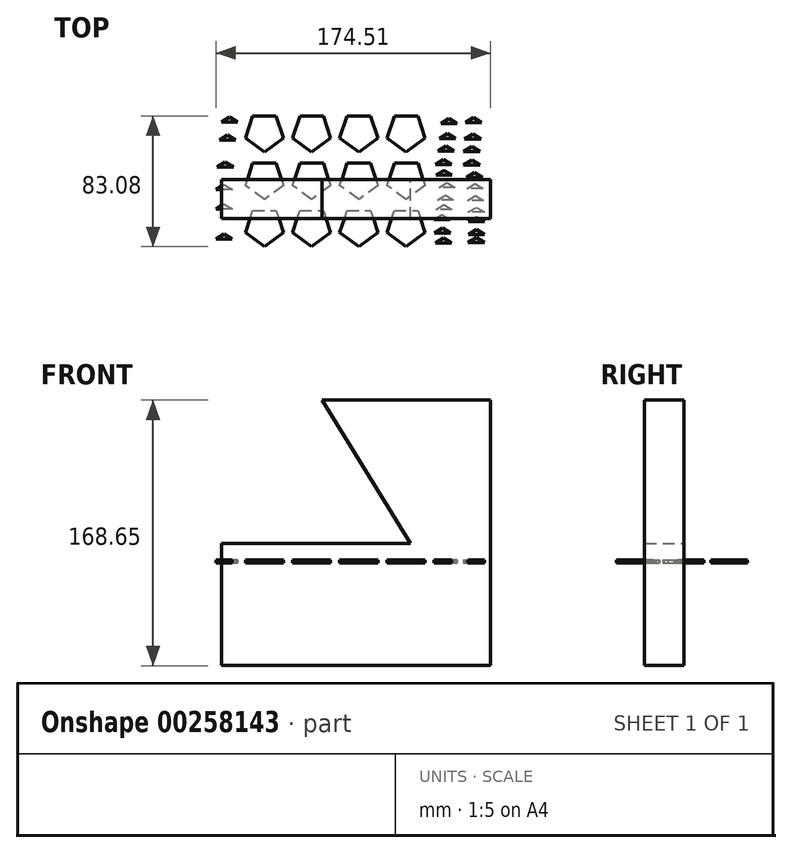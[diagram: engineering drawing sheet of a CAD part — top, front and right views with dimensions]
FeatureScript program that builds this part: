
annotation { "Feature Type Name" : "Feature", "Feature Type Description" : "" }
export const myFeature = defineFeature(function(context is Context, id is Id, definition is map)
    precondition{}
    {
        {
            var Q0;
            Q0=qCreatedBy(makeId("Top.planeOp"),FACE);
            var sketch = newSketch(context, id + "F0", { "sketchPlane" : qUnion([Q0])});
            skCircle(sketch, "E0.cCircle", {"center": v(30, 30) * mm, "radius": 10.32 * mm, "construction": true});
            skLineSegment(sketch, "E0.0", {"start": v(22.5, 40.32) * mm, "end": v(37.5, 40.32) * mm});
            skLineSegment(sketch, "E0.1", {"start": v(37.5, 40.32) * mm, "end": v(42.14, 26.06) * mm});
            skLineSegment(sketch, "E0.2", {"start": v(42.14, 26.06) * mm, "end": v(30, 17.24) * mm});
            skLineSegment(sketch, "E0.3", {"start": v(30, 17.24) * mm, "end": v(17.86, 26.06) * mm});
            skLineSegment(sketch, "E0.4", {"start": v(17.86, 26.06) * mm, "end": v(22.5, 40.32) * mm});
            skPoint(sketch, "E0.0.midPoint", {"position": v(30, 40.32) * mm});
            skLineSegment(sketch, "E1", {"start": v(52.02, 35.35) * mm, "end": v(57.12, 38.5) * mm});
            skLineSegment(sketch, "E2", {"start": v(57.12, 38.5) * mm, "end": v(62.23, 35.35) * mm});
            skLineSegment(sketch, "E3", {"start": v(62.23, 35.35) * mm, "end": v(52.02, 35.35) * mm});
            skCircle(sketch, "E4.cCircle", {"center": v(-60, 30) * mm, "radius": 10.32 * mm, "construction": true});
            skLineSegment(sketch, "E4.0", {"start": v(-67.5, 40.32) * mm, "end": v(-52.5, 40.32) * mm});
            skLineSegment(sketch, "E4.1", {"start": v(-52.5, 40.32) * mm, "end": v(-47.86, 26.06) * mm});
            skLineSegment(sketch, "E4.2", {"start": v(-47.86, 26.06) * mm, "end": v(-60, 17.24) * mm});
            skLineSegment(sketch, "E4.3", {"start": v(-60, 17.24) * mm, "end": v(-72.14, 26.06) * mm});
            skLineSegment(sketch, "E4.4", {"start": v(-72.14, 26.06) * mm, "end": v(-67.5, 40.32) * mm});
            skPoint(sketch, "E4.0.midPoint", {"position": v(-60, 40.32) * mm});
            skCircle(sketch, "E5.cCircle", {"center": v(-30, 30) * mm, "radius": 10.32 * mm, "construction": true});
            skLineSegment(sketch, "E5.0", {"start": v(-37.5, 40.32) * mm, "end": v(-22.5, 40.32) * mm});
            skLineSegment(sketch, "E5.1", {"start": v(-22.5, 40.32) * mm, "end": v(-17.86, 26.06) * mm});
            skLineSegment(sketch, "E5.2", {"start": v(-17.86, 26.06) * mm, "end": v(-30, 17.24) * mm});
            skLineSegment(sketch, "E5.3", {"start": v(-30, 17.24) * mm, "end": v(-42.14, 26.06) * mm});
            skLineSegment(sketch, "E5.4", {"start": v(-42.14, 26.06) * mm, "end": v(-37.5, 40.32) * mm});
            skPoint(sketch, "E5.0.midPoint", {"position": v(-30, 40.32) * mm});
            skCircle(sketch, "E6.cCircle", {"center": v(0, 30) * mm, "radius": 10.32 * mm, "construction": true});
            skLineSegment(sketch, "E6.0", {"start": v(-7.5, 40.32) * mm, "end": v(7.5, 40.32) * mm});
            skLineSegment(sketch, "E6.1", {"start": v(7.5, 40.32) * mm, "end": v(12.14, 26.06) * mm});
            skLineSegment(sketch, "E6.2", {"start": v(12.14, 26.06) * mm, "end": v(0, 17.24) * mm});
            skLineSegment(sketch, "E6.3", {"start": v(0, 17.24) * mm, "end": v(-12.14, 26.06) * mm});
            skLineSegment(sketch, "E6.4", {"start": v(-12.14, 26.06) * mm, "end": v(-7.5, 40.32) * mm});
            skPoint(sketch, "E6.0.midPoint", {"position": v(0, 40.32) * mm});
            skLineSegment(sketch, "E7", {"start": v(-30, 111.24) * mm, "end": v(-30, -87.7) * mm, "construction": true});
            skLineSegment(sketch, "E8", {"start": v(30, 123) * mm, "end": v(30, -85) * mm, "construction": true});
            skLineSegment(sketch, "E9", {"start": v(-60, 78.46) * mm, "end": v(-60, -80.93) * mm, "construction": true});
            skLineSegment(sketch, "E10", {"start": v(-144.87, 30) * mm, "end": v(60.05, 30) * mm, "construction": true});
            skLineSegment(sketch, "E11", {"start": v(-120.62, -30) * mm, "end": v(95.14, -30) * mm, "construction": true});
            skCircle(sketch, "E12.cCircle", {"center": v(-60, 0) * mm, "radius": 10.32 * mm, "construction": true});
            skLineSegment(sketch, "E12.0", {"start": v(-67.5, 10.32) * mm, "end": v(-52.5, 10.32) * mm});
            skLineSegment(sketch, "E12.1", {"start": v(-52.5, 10.32) * mm, "end": v(-47.86, -3.94) * mm});
            skLineSegment(sketch, "E12.2", {"start": v(-47.86, -3.94) * mm, "end": v(-60, -12.76) * mm});
            skLineSegment(sketch, "E12.3", {"start": v(-60, -12.76) * mm, "end": v(-72.14, -3.94) * mm});
            skLineSegment(sketch, "E12.4", {"start": v(-72.14, -3.94) * mm, "end": v(-67.5, 10.32) * mm});
            skCircle(sketch, "E13.cCircle", {"center": v(0, 0) * mm, "radius": 10.32 * mm, "construction": true});
            skLineSegment(sketch, "E13.0", {"start": v(-7.5, 10.32) * mm, "end": v(7.5, 10.32) * mm});
            skLineSegment(sketch, "E13.1", {"start": v(7.5, 10.32) * mm, "end": v(12.14, -3.94) * mm});
            skLineSegment(sketch, "E13.2", {"start": v(12.14, -3.94) * mm, "end": v(0, -12.76) * mm});
            skLineSegment(sketch, "E13.3", {"start": v(0, -12.76) * mm, "end": v(-12.14, -3.94) * mm});
            skLineSegment(sketch, "E13.4", {"start": v(-12.14, -3.94) * mm, "end": v(-7.5, 10.32) * mm});
            skCircle(sketch, "E14.cCircle", {"center": v(-60, -30) * mm, "radius": 10.32 * mm, "construction": true});
            skLineSegment(sketch, "E14.0", {"start": v(-67.5, -19.68) * mm, "end": v(-52.5, -19.68) * mm});
            skLineSegment(sketch, "E14.1", {"start": v(-52.5, -19.68) * mm, "end": v(-47.86, -33.94) * mm});
            skLineSegment(sketch, "E14.2", {"start": v(-47.86, -33.94) * mm, "end": v(-60, -42.76) * mm});
            skLineSegment(sketch, "E14.3", {"start": v(-60, -42.76) * mm, "end": v(-72.14, -33.94) * mm});
            skLineSegment(sketch, "E14.4", {"start": v(-72.14, -33.94) * mm, "end": v(-67.5, -19.68) * mm});
            skCircle(sketch, "E15.cCircle", {"center": v(-30, -30) * mm, "radius": 10.32 * mm, "construction": true});
            skLineSegment(sketch, "E15.0", {"start": v(-37.5, -19.68) * mm, "end": v(-22.5, -19.68) * mm});
            skLineSegment(sketch, "E15.1", {"start": v(-22.5, -19.68) * mm, "end": v(-17.86, -33.94) * mm});
            skLineSegment(sketch, "E15.2", {"start": v(-17.86, -33.94) * mm, "end": v(-30, -42.76) * mm});
            skLineSegment(sketch, "E15.3", {"start": v(-30, -42.76) * mm, "end": v(-42.14, -33.94) * mm});
            skLineSegment(sketch, "E15.4", {"start": v(-42.14, -33.94) * mm, "end": v(-37.5, -19.68) * mm});
            skCircle(sketch, "E16.cCircle", {"center": v(-30, 0) * mm, "radius": 10.32 * mm, "construction": true});
            skLineSegment(sketch, "E16.0", {"start": v(-37.5, 10.32) * mm, "end": v(-22.5, 10.32) * mm});
            skLineSegment(sketch, "E16.1", {"start": v(-22.5, 10.32) * mm, "end": v(-17.86, -3.94) * mm});
            skLineSegment(sketch, "E16.2", {"start": v(-17.86, -3.94) * mm, "end": v(-30, -12.76) * mm});
            skLineSegment(sketch, "E16.3", {"start": v(-30, -12.76) * mm, "end": v(-42.14, -3.94) * mm});
            skLineSegment(sketch, "E16.4", {"start": v(-42.14, -3.94) * mm, "end": v(-37.5, 10.32) * mm});
            skCircle(sketch, "E17.cCircle", {"center": v(30, 0) * mm, "radius": 10.32 * mm, "construction": true});
            skLineSegment(sketch, "E17.0", {"start": v(22.5, 10.32) * mm, "end": v(37.5, 10.32) * mm});
            skLineSegment(sketch, "E17.1", {"start": v(37.5, 10.32) * mm, "end": v(42.14, -3.94) * mm});
            skLineSegment(sketch, "E17.2", {"start": v(42.14, -3.94) * mm, "end": v(30, -12.76) * mm});
            skLineSegment(sketch, "E17.3", {"start": v(30, -12.76) * mm, "end": v(17.86, -3.94) * mm});
            skLineSegment(sketch, "E17.4", {"start": v(17.86, -3.94) * mm, "end": v(22.5, 10.32) * mm});
            skCircle(sketch, "E18.cCircle", {"center": v(30, -30) * mm, "radius": 10.32 * mm, "construction": true});
            skLineSegment(sketch, "E18.0", {"start": v(22.5, -19.68) * mm, "end": v(37.5, -19.68) * mm});
            skLineSegment(sketch, "E18.1", {"start": v(37.5, -19.68) * mm, "end": v(42.14, -33.94) * mm});
            skLineSegment(sketch, "E18.2", {"start": v(42.14, -33.94) * mm, "end": v(30, -42.76) * mm});
            skLineSegment(sketch, "E18.3", {"start": v(30, -42.76) * mm, "end": v(17.86, -33.94) * mm});
            skLineSegment(sketch, "E18.4", {"start": v(17.86, -33.94) * mm, "end": v(22.5, -19.68) * mm});
            skCircle(sketch, "E19.cCircle", {"center": v(0, -30) * mm, "radius": 10.32 * mm, "construction": true});
            skLineSegment(sketch, "E19.0", {"start": v(-7.5, -19.68) * mm, "end": v(7.5, -19.68) * mm});
            skLineSegment(sketch, "E19.1", {"start": v(7.5, -19.68) * mm, "end": v(12.14, -33.94) * mm});
            skLineSegment(sketch, "E19.2", {"start": v(12.14, -33.94) * mm, "end": v(0, -42.76) * mm});
            skLineSegment(sketch, "E19.3", {"start": v(0, -42.76) * mm, "end": v(-12.14, -33.94) * mm});
            skLineSegment(sketch, "E19.4", {"start": v(-12.14, -33.94) * mm, "end": v(-7.5, -19.68) * mm});
            skLineSegment(sketch, "E20", {"start": v(67.72, 36.11) * mm, "end": v(72.83, 39.27) * mm});
            skLineSegment(sketch, "E21", {"start": v(72.83, 39.27) * mm, "end": v(77.93, 36.11) * mm});
            skLineSegment(sketch, "E22", {"start": v(77.93, 36.11) * mm, "end": v(67.72, 36.11) * mm});
            skLineSegment(sketch, "E23", {"start": v(51.27, 25.89) * mm, "end": v(56.37, 29.04) * mm});
            skLineSegment(sketch, "E24", {"start": v(56.37, 29.04) * mm, "end": v(61.48, 25.89) * mm});
            skLineSegment(sketch, "E25", {"start": v(61.48, 25.89) * mm, "end": v(51.27, 25.89) * mm});
            skLineSegment(sketch, "E26", {"start": v(67.25, 25.57) * mm, "end": v(72.35, 28.72) * mm});
            skLineSegment(sketch, "E27", {"start": v(72.35, 28.72) * mm, "end": v(77.45, 25.57) * mm});
            skLineSegment(sketch, "E28", {"start": v(77.45, 25.57) * mm, "end": v(67.25, 25.57) * mm});
            skLineSegment(sketch, "E29", {"start": v(50.31, 18.06) * mm, "end": v(55.41, 21.22) * mm});
            skLineSegment(sketch, "E30", {"start": v(55.41, 21.22) * mm, "end": v(60.52, 18.06) * mm});
            skLineSegment(sketch, "E31", {"start": v(60.52, 18.06) * mm, "end": v(50.31, 18.06) * mm});
            skLineSegment(sketch, "E32", {"start": v(66.6, 17.74) * mm, "end": v(71.7, 20.9) * mm});
            skLineSegment(sketch, "E33", {"start": v(71.7, 20.9) * mm, "end": v(76.81, 17.74) * mm});
            skLineSegment(sketch, "E34", {"start": v(76.81, 17.74) * mm, "end": v(66.6, 17.74) * mm});
            skLineSegment(sketch, "E35", {"start": v(48.71, 9.43) * mm, "end": v(53.82, 12.59) * mm});
            skLineSegment(sketch, "E36", {"start": v(53.82, 12.59) * mm, "end": v(58.92, 9.43) * mm});
            skLineSegment(sketch, "E37", {"start": v(58.92, 9.43) * mm, "end": v(48.71, 9.43) * mm});
            skLineSegment(sketch, "E38", {"start": v(66.6, 8.96) * mm, "end": v(71.7, 12.1) * mm});
            skLineSegment(sketch, "E39", {"start": v(71.7, 12.1) * mm, "end": v(76.81, 8.96) * mm});
            skLineSegment(sketch, "E40", {"start": v(76.81, 8.96) * mm, "end": v(66.6, 8.96) * mm});
            skLineSegment(sketch, "E41", {"start": v(48.87, 2.57) * mm, "end": v(53.98, 5.72) * mm});
            skLineSegment(sketch, "E42", {"start": v(53.98, 5.72) * mm, "end": v(59.08, 2.57) * mm});
            skLineSegment(sketch, "E43", {"start": v(59.08, 2.57) * mm, "end": v(48.87, 2.57) * mm});
            skLineSegment(sketch, "E44", {"start": v(68.36, 1.13) * mm, "end": v(73.47, 4.28) * mm});
            skLineSegment(sketch, "E45", {"start": v(73.47, 4.28) * mm, "end": v(78.57, 1.13) * mm});
            skLineSegment(sketch, "E46", {"start": v(78.57, 1.13) * mm, "end": v(68.36, 1.13) * mm});
            skLineSegment(sketch, "E47", {"start": v(50.79, -5.1) * mm, "end": v(55.9, -1.95) * mm});
            skLineSegment(sketch, "E48", {"start": v(55.9, -1.95) * mm, "end": v(61, -5.1) * mm});
            skLineSegment(sketch, "E49", {"start": v(61, -5.1) * mm, "end": v(50.79, -5.1) * mm});
            skLineSegment(sketch, "E50", {"start": v(68.52, -5.74) * mm, "end": v(73.63, -2.59) * mm});
            skLineSegment(sketch, "E51", {"start": v(73.63, -2.59) * mm, "end": v(78.73, -5.74) * mm});
            skLineSegment(sketch, "E52", {"start": v(78.73, -5.74) * mm, "end": v(68.52, -5.74) * mm});
            skLineSegment(sketch, "E53", {"start": v(49.83, -13.25) * mm, "end": v(54.94, -10.1) * mm});
            skLineSegment(sketch, "E54", {"start": v(54.94, -10.1) * mm, "end": v(60.04, -13.25) * mm});
            skLineSegment(sketch, "E55", {"start": v(60.04, -13.25) * mm, "end": v(49.83, -13.25) * mm});
            skLineSegment(sketch, "E56", {"start": v(69, -13.41) * mm, "end": v(74.1, -10.26) * mm});
            skLineSegment(sketch, "E57", {"start": v(74.1, -10.26) * mm, "end": v(79.2, -13.41) * mm});
            skLineSegment(sketch, "E58", {"start": v(79.2, -13.41) * mm, "end": v(69, -13.41) * mm});
            skLineSegment(sketch, "E59", {"start": v(49.03, -19.16) * mm, "end": v(54.14, -16) * mm});
            skLineSegment(sketch, "E60", {"start": v(54.14, -16) * mm, "end": v(59.24, -19.16) * mm});
            skLineSegment(sketch, "E61", {"start": v(59.24, -19.16) * mm, "end": v(49.03, -19.16) * mm});
            skLineSegment(sketch, "E62", {"start": v(69.48, -20.92) * mm, "end": v(74.59, -17.76) * mm});
            skLineSegment(sketch, "E63", {"start": v(74.59, -17.76) * mm, "end": v(79.69, -20.92) * mm});
            skLineSegment(sketch, "E64", {"start": v(79.69, -20.92) * mm, "end": v(69.48, -20.92) * mm});
            skLineSegment(sketch, "E65", {"start": v(47.6, -25.55) * mm, "end": v(52.7, -22.4) * mm});
            skLineSegment(sketch, "E66", {"start": v(52.7, -22.4) * mm, "end": v(57.8, -25.55) * mm});
            skLineSegment(sketch, "E67", {"start": v(57.8, -25.55) * mm, "end": v(47.6, -25.55) * mm});
            skLineSegment(sketch, "E68", {"start": v(69.64, -26.83) * mm, "end": v(74.75, -23.68) * mm});
            skLineSegment(sketch, "E69", {"start": v(74.75, -23.68) * mm, "end": v(79.85, -26.83) * mm});
            skLineSegment(sketch, "E70", {"start": v(79.85, -26.83) * mm, "end": v(69.64, -26.83) * mm});
            skLineSegment(sketch, "E71", {"start": v(47.91, -34.02) * mm, "end": v(53.02, -30.87) * mm});
            skLineSegment(sketch, "E72", {"start": v(53.02, -30.87) * mm, "end": v(58.12, -34.02) * mm});
            skLineSegment(sketch, "E73", {"start": v(58.12, -34.02) * mm, "end": v(47.91, -34.02) * mm});
            skLineSegment(sketch, "E74", {"start": v(69.64, -35.14) * mm, "end": v(74.75, -31.98) * mm});
            skLineSegment(sketch, "E75", {"start": v(74.75, -31.98) * mm, "end": v(79.85, -35.14) * mm});
            skLineSegment(sketch, "E76", {"start": v(79.85, -35.14) * mm, "end": v(69.64, -35.14) * mm});
            skLineSegment(sketch, "E77", {"start": v(48.71, -40.4) * mm, "end": v(53.82, -37.26) * mm});
            skLineSegment(sketch, "E78", {"start": v(53.82, -37.26) * mm, "end": v(58.92, -40.4) * mm});
            skLineSegment(sketch, "E79", {"start": v(58.92, -40.4) * mm, "end": v(48.71, -40.4) * mm});
            skLineSegment(sketch, "E80", {"start": v(69.48, -40.25) * mm, "end": v(74.59, -37.1) * mm});
            skLineSegment(sketch, "E81", {"start": v(74.59, -37.1) * mm, "end": v(79.69, -40.25) * mm});
            skLineSegment(sketch, "E82", {"start": v(79.69, -40.25) * mm, "end": v(69.48, -40.25) * mm});
            skLineSegment(sketch, "E83", {"start": v(-87.24, 36.27) * mm, "end": v(-82.14, 39.43) * mm});
            skLineSegment(sketch, "E84", {"start": v(-82.14, 39.43) * mm, "end": v(-77.03, 36.27) * mm});
            skLineSegment(sketch, "E85", {"start": v(-77.03, 36.27) * mm, "end": v(-87.24, 36.27) * mm});
            skLineSegment(sketch, "E86", {"start": v(-88.36, 25.1) * mm, "end": v(-83.26, 28.25) * mm});
            skLineSegment(sketch, "E87", {"start": v(-83.26, 28.25) * mm, "end": v(-78.15, 25.1) * mm});
            skLineSegment(sketch, "E88", {"start": v(-78.15, 25.1) * mm, "end": v(-88.36, 25.1) * mm});
            skLineSegment(sketch, "E89", {"start": v(-89.96, 7.68) * mm, "end": v(-84.85, 10.83) * mm});
            skLineSegment(sketch, "E90", {"start": v(-84.85, 10.83) * mm, "end": v(-79.75, 7.68) * mm});
            skLineSegment(sketch, "E91", {"start": v(-79.75, 7.68) * mm, "end": v(-89.96, 7.68) * mm});
            skLineSegment(sketch, "E92", {"start": v(-90.6, -6.54) * mm, "end": v(-85.5, -3.39) * mm});
            skLineSegment(sketch, "E93", {"start": v(-85.5, -3.39) * mm, "end": v(-80.39, -6.54) * mm});
            skLineSegment(sketch, "E94", {"start": v(-80.39, -6.54) * mm, "end": v(-90.6, -6.54) * mm});
            skLineSegment(sketch, "E95", {"start": v(-90.6, -18.84) * mm, "end": v(-85.5, -15.69) * mm});
            skLineSegment(sketch, "E96", {"start": v(-85.5, -15.69) * mm, "end": v(-80.39, -18.84) * mm});
            skLineSegment(sketch, "E97", {"start": v(-80.39, -18.84) * mm, "end": v(-90.6, -18.84) * mm});
            skLineSegment(sketch, "E98", {"start": v(-90.76, -37.85) * mm, "end": v(-85.65, -34.7) * mm});
            skLineSegment(sketch, "E99", {"start": v(-85.65, -34.7) * mm, "end": v(-80.55, -37.85) * mm});
            skLineSegment(sketch, "E100", {"start": v(-80.55, -37.85) * mm, "end": v(-90.76, -37.85) * mm});
            skSolve(sketch);
        }
        {
            var Q0;
            Q0=makeQuery(id+"F0.imprint","IMPRINT",FACE,{"disambiguationData":[TD([[makeQuery(id+"F0.imprint","IMPRINT",EDGE,{"derivedFrom":sQuery(id+"F0.wireOp",EDGE,"E83")}),-1.0]])]});
            var Q1;
            Q1=makeQuery(id+"F0.imprint","IMPRINT",FACE,{"disambiguationData":[TD([[makeQuery(id+"F0.imprint","IMPRINT",EDGE,{"derivedFrom":sQuery(id+"F0.wireOp",EDGE,"E4.0")}),-1.0]])]});
            var Q2;
            Q2=makeQuery(id+"F0.imprint","IMPRINT",FACE,{"disambiguationData":[TD([[makeQuery(id+"F0.imprint","IMPRINT",EDGE,{"derivedFrom":sQuery(id+"F0.wireOp",EDGE,"E5.0")}),-1.0]])]});
            var Q3;
            Q3=makeQuery(id+"F0.imprint","IMPRINT",FACE,{"disambiguationData":[TD([[makeQuery(id+"F0.imprint","IMPRINT",EDGE,{"derivedFrom":sQuery(id+"F0.wireOp",EDGE,"E6.0")}),-1.0]])]});
            var Q4;
            Q4=makeQuery(id+"F0.imprint","IMPRINT",FACE,{"disambiguationData":[TD([[makeQuery(id+"F0.imprint","IMPRINT",EDGE,{"derivedFrom":sQuery(id+"F0.wireOp",EDGE,"E0.0")}),-1.0]])]});
            var Q5;
            Q5=makeQuery(id+"F0.imprint","IMPRINT",FACE,{"disambiguationData":[TD([[makeQuery(id+"F0.imprint","IMPRINT",EDGE,{"derivedFrom":sQuery(id+"F0.wireOp",EDGE,"E17.0")}),-1.0]])]});
            var Q6;
            Q6=makeQuery(id+"F0.imprint","IMPRINT",FACE,{"disambiguationData":[TD([[makeQuery(id+"F0.imprint","IMPRINT",EDGE,{"derivedFrom":sQuery(id+"F0.wireOp",EDGE,"E13.0")}),-1.0]])]});
            var Q7;
            Q7=makeQuery(id+"F0.imprint","IMPRINT",FACE,{"disambiguationData":[TD([[makeQuery(id+"F0.imprint","IMPRINT",EDGE,{"derivedFrom":sQuery(id+"F0.wireOp",EDGE,"E16.0")}),-1.0]])]});
            var Q8;
            Q8=makeQuery(id+"F0.imprint","IMPRINT",FACE,{"disambiguationData":[TD([[makeQuery(id+"F0.imprint","IMPRINT",EDGE,{"derivedFrom":sQuery(id+"F0.wireOp",EDGE,"E12.0")}),-1.0]])]});
            var Q9;
            Q9=makeQuery(id+"F0.imprint","IMPRINT",FACE,{"disambiguationData":[TD([[makeQuery(id+"F0.imprint","IMPRINT",EDGE,{"derivedFrom":sQuery(id+"F0.wireOp",EDGE,"E14.0")}),-1.0]])]});
            var Q10;
            Q10=makeQuery(id+"F0.imprint","IMPRINT",FACE,{"disambiguationData":[TD([[makeQuery(id+"F0.imprint","IMPRINT",EDGE,{"derivedFrom":sQuery(id+"F0.wireOp",EDGE,"E15.0")}),-1.0]])]});
            var Q11;
            Q11=makeQuery(id+"F0.imprint","IMPRINT",FACE,{"disambiguationData":[TD([[makeQuery(id+"F0.imprint","IMPRINT",EDGE,{"derivedFrom":sQuery(id+"F0.wireOp",EDGE,"E19.0")}),-1.0]])]});
            var Q12;
            Q12=makeQuery(id+"F0.imprint","IMPRINT",FACE,{"disambiguationData":[TD([[makeQuery(id+"F0.imprint","IMPRINT",EDGE,{"derivedFrom":sQuery(id+"F0.wireOp",EDGE,"E18.0")}),-1.0]])]});
            var Q13;
            Q13=makeQuery(id+"F0.imprint","IMPRINT",FACE,{"disambiguationData":[TD([[makeQuery(id+"F0.imprint","IMPRINT",EDGE,{"derivedFrom":sQuery(id+"F0.wireOp",EDGE,"E86")}),-1.0]])]});
            var Q14;
            Q14=makeQuery(id+"F0.imprint","IMPRINT",FACE,{"disambiguationData":[TD([[makeQuery(id+"F0.imprint","IMPRINT",EDGE,{"derivedFrom":sQuery(id+"F0.wireOp",EDGE,"E89")}),-1.0]])]});
            var Q15;
            Q15=makeQuery(id+"F0.imprint","IMPRINT",FACE,{"disambiguationData":[TD([[makeQuery(id+"F0.imprint","IMPRINT",EDGE,{"derivedFrom":sQuery(id+"F0.wireOp",EDGE,"E92")}),-1.0]])]});
            var Q16;
            Q16=makeQuery(id+"F0.imprint","IMPRINT",FACE,{"disambiguationData":[TD([[makeQuery(id+"F0.imprint","IMPRINT",EDGE,{"derivedFrom":sQuery(id+"F0.wireOp",EDGE,"E95")}),-1.0]])]});
            var Q17;
            Q17=makeQuery(id+"F0.imprint","IMPRINT",FACE,{"disambiguationData":[TD([[makeQuery(id+"F0.imprint","IMPRINT",EDGE,{"derivedFrom":sQuery(id+"F0.wireOp",EDGE,"E98")}),-1.0]])]});
            var Q18;
            Q18=makeQuery(id+"F0.imprint","IMPRINT",FACE,{"disambiguationData":[TD([[makeQuery(id+"F0.imprint","IMPRINT",EDGE,{"derivedFrom":sQuery(id+"F0.wireOp",EDGE,"E80")}),-1.0]])]});
            var Q19;
            Q19=makeQuery(id+"F0.imprint","IMPRINT",FACE,{"disambiguationData":[TD([[makeQuery(id+"F0.imprint","IMPRINT",EDGE,{"derivedFrom":sQuery(id+"F0.wireOp",EDGE,"E77")}),-1.0]])]});
            var Q20;
            Q20=makeQuery(id+"F0.imprint","IMPRINT",FACE,{"disambiguationData":[TD([[makeQuery(id+"F0.imprint","IMPRINT",EDGE,{"derivedFrom":sQuery(id+"F0.wireOp",EDGE,"E71")}),-1.0]])]});
            var Q21;
            Q21=makeQuery(id+"F0.imprint","IMPRINT",FACE,{"disambiguationData":[TD([[makeQuery(id+"F0.imprint","IMPRINT",EDGE,{"derivedFrom":sQuery(id+"F0.wireOp",EDGE,"E74")}),-1.0]])]});
            var Q22;
            Q22=makeQuery(id+"F0.imprint","IMPRINT",FACE,{"disambiguationData":[TD([[makeQuery(id+"F0.imprint","IMPRINT",EDGE,{"derivedFrom":sQuery(id+"F0.wireOp",EDGE,"E68")}),-1.0]])]});
            var Q23;
            Q23=makeQuery(id+"F0.imprint","IMPRINT",FACE,{"disambiguationData":[TD([[makeQuery(id+"F0.imprint","IMPRINT",EDGE,{"derivedFrom":sQuery(id+"F0.wireOp",EDGE,"E65")}),-1.0]])]});
            var Q24;
            Q24=makeQuery(id+"F0.imprint","IMPRINT",FACE,{"disambiguationData":[TD([[makeQuery(id+"F0.imprint","IMPRINT",EDGE,{"derivedFrom":sQuery(id+"F0.wireOp",EDGE,"E59")}),-1.0]])]});
            var Q25;
            Q25=makeQuery(id+"F0.imprint","IMPRINT",FACE,{"disambiguationData":[TD([[makeQuery(id+"F0.imprint","IMPRINT",EDGE,{"derivedFrom":sQuery(id+"F0.wireOp",EDGE,"E62")}),-1.0]])]});
            var Q26;
            Q26=makeQuery(id+"F0.imprint","IMPRINT",FACE,{"disambiguationData":[TD([[makeQuery(id+"F0.imprint","IMPRINT",EDGE,{"derivedFrom":sQuery(id+"F0.wireOp",EDGE,"E53")}),-1.0]])]});
            var Q27;
            Q27=makeQuery(id+"F0.imprint","IMPRINT",FACE,{"disambiguationData":[TD([[makeQuery(id+"F0.imprint","IMPRINT",EDGE,{"derivedFrom":sQuery(id+"F0.wireOp",EDGE,"E56")}),-1.0]])]});
            var Q28;
            Q28=makeQuery(id+"F0.imprint","IMPRINT",FACE,{"disambiguationData":[TD([[makeQuery(id+"F0.imprint","IMPRINT",EDGE,{"derivedFrom":sQuery(id+"F0.wireOp",EDGE,"E50")}),-1.0]])]});
            var Q29;
            Q29=makeQuery(id+"F0.imprint","IMPRINT",FACE,{"disambiguationData":[TD([[makeQuery(id+"F0.imprint","IMPRINT",EDGE,{"derivedFrom":sQuery(id+"F0.wireOp",EDGE,"E47")}),-1.0]])]});
            var Q30;
            Q30=makeQuery(id+"F0.imprint","IMPRINT",FACE,{"disambiguationData":[TD([[makeQuery(id+"F0.imprint","IMPRINT",EDGE,{"derivedFrom":sQuery(id+"F0.wireOp",EDGE,"E41")}),-1.0]])]});
            var Q31;
            Q31=makeQuery(id+"F0.imprint","IMPRINT",FACE,{"disambiguationData":[TD([[makeQuery(id+"F0.imprint","IMPRINT",EDGE,{"derivedFrom":sQuery(id+"F0.wireOp",EDGE,"E44")}),-1.0]])]});
            var Q32;
            Q32=makeQuery(id+"F0.imprint","IMPRINT",FACE,{"disambiguationData":[TD([[makeQuery(id+"F0.imprint","IMPRINT",EDGE,{"derivedFrom":sQuery(id+"F0.wireOp",EDGE,"E38")}),-1.0]])]});
            var Q33;
            Q33=makeQuery(id+"F0.imprint","IMPRINT",FACE,{"disambiguationData":[TD([[makeQuery(id+"F0.imprint","IMPRINT",EDGE,{"derivedFrom":sQuery(id+"F0.wireOp",EDGE,"E35")}),-1.0]])]});
            var Q34;
            Q34=makeQuery(id+"F0.imprint","IMPRINT",FACE,{"disambiguationData":[TD([[makeQuery(id+"F0.imprint","IMPRINT",EDGE,{"derivedFrom":sQuery(id+"F0.wireOp",EDGE,"E29")}),-1.0]])]});
            var Q35;
            Q35=makeQuery(id+"F0.imprint","IMPRINT",FACE,{"disambiguationData":[TD([[makeQuery(id+"F0.imprint","IMPRINT",EDGE,{"derivedFrom":sQuery(id+"F0.wireOp",EDGE,"E32")}),-1.0]])]});
            var Q36;
            Q36=makeQuery(id+"F0.imprint","IMPRINT",FACE,{"disambiguationData":[TD([[makeQuery(id+"F0.imprint","IMPRINT",EDGE,{"derivedFrom":sQuery(id+"F0.wireOp",EDGE,"E26")}),-1.0]])]});
            var Q37;
            Q37=makeQuery(id+"F0.imprint","IMPRINT",FACE,{"disambiguationData":[TD([[makeQuery(id+"F0.imprint","IMPRINT",EDGE,{"derivedFrom":sQuery(id+"F0.wireOp",EDGE,"E23")}),-1.0]])]});
            var Q38;
            Q38=makeQuery(id+"F0.imprint","IMPRINT",FACE,{"disambiguationData":[TD([[makeQuery(id+"F0.imprint","IMPRINT",EDGE,{"derivedFrom":sQuery(id+"F0.wireOp",EDGE,"E20")}),-1.0]])]});
            var Q39;
            Q39=makeQuery(id+"F0.imprint","IMPRINT",FACE,{"disambiguationData":[TD([[makeQuery(id+"F0.imprint","IMPRINT",EDGE,{"derivedFrom":sQuery(id+"F0.wireOp",EDGE,"E1")}),-1.0]])]});
            extrude(context, id + "F1", {"entities" : qUnion([Q0, Q1, Q2, Q3, Q4, Q5, Q6, Q7, Q8, Q9, Q10, Q11, Q12, Q13, Q14, Q15, Q16, Q17, Q18, Q19, Q20, Q21, Q22, Q23, Q24, Q25, Q26, Q27, Q28, Q29, Q30, Q31, Q32, Q33, Q34, Q35, Q36, Q37, Q38, Q39]), "depth" : 2 * mm});
        }
        {
            var Q0;
            Q0=qCreatedBy(makeId("Front.planeOp"),FACE);
            var sketch = newSketch(context, id + "F2", { "sketchPlane" : qUnion([Q0])});
            skLineSegment(sketch, "E101", {"start": v(-87.12, 12.52) * mm, "end": v(32.88, 12.52) * mm});
            skLineSegment(sketch, "E102", {"start": v(32.88, 12.52) * mm, "end": v(-23.4, 103.56) * mm});
            skLineSegment(sketch, "E103", {"start": v(-23.4, 103.56) * mm, "end": v(83.75, 103.56) * mm});
            skLineSegment(sketch, "E104", {"start": v(83.75, 103.56) * mm, "end": v(83.75, -65.09) * mm});
            skLineSegment(sketch, "E105", {"start": v(83.75, -65.09) * mm, "end": v(-87.12, -65.09) * mm});
            skLineSegment(sketch, "E106", {"start": v(-87.12, -65.09) * mm, "end": v(-87.12, 12.52) * mm});
            skSolve(sketch);
        }
        {
            var Q0;
            Q0=makeQuery(id+"F2.imprint","IMPRINT",FACE,{"disambiguationData":[TD([[makeQuery(id+"F2.imprint","IMPRINT",EDGE,{"derivedFrom":sQuery(id+"F2.wireOp",EDGE,"E101")}),-1.0]])]});
            extrude(context, id + "F3", {"entities" : qUnion([Q0]), "depth" : 25 * mm});
        }
    });
